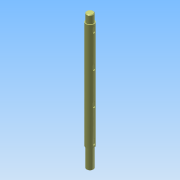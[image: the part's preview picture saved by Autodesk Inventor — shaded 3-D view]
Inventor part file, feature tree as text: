
AUTODESK INVENTOR PART (.ipt)
format: ipt  version: 2015 (Build 190159000, 159)  size: 145,920 bytes
history: native  units: mm
features: extrude x4, sketch x4, plane x1, pattern_linear x1, fillet x1, chamfer x1
ambient origin geometry x8: Origin, YZ Plane, XZ Plane, XY Plane, X Axis, Y Axis, Z Axis, Center Point
bodies: 实体1 (feature_tree)
feature tree (12):
  extrude  "拉伸1"  Depth=398.0mm TaperAngle=0.0deg
  plane  "工作平面1"
  extrude  "拉伸2"  Depth=8.0mm
  pattern_linear  "矩形阵列1"  Spacing1=3.0mm  [1 undecoded]
  fillet  "圆角1"  Radius=40.0mm
  extrude  "拉伸3"  Depth=0.5mm
  extrude  "拉伸4"  Depth=30.0mm
  chamfer  "倒角1"  Distance=71.0mm
  sketch  "草图1"  dims[d0=30.0mm d1=398.0mm d2=0.0mm]
  sketch  "草图2"  dims[d3=8.0mm d4=14.0mm]
  sketch  "草图3"  dims[d5=0.0mm]
  sketch  "草图4"  dims[d6=12.0mm d7=3.0mm d8=0.0mm d9=40.0mm d11=120.0mm d12=0.5mm d13=25.0mm d14=71.0mm d15=0.0mm d16=25.0mm d17=30.0mm d18=0.0mm d19=2.0mm d20=2.0mm d21=45.0deg]
note: 1 required parameter value undecoded (feature->parameter linkage not recoverable at this tier; creation-order binding heuristic only, values carry confidence <= 0.55)
